# Revit family: Shower-Wall_Supply_Elbow-KOHLER-BEITOU-K-26310T
name_source: partatom
category: Plumbing Fixtures
revit_build: Autodesk Revit 2017 (Build: 20160225_1515(x64)
units: mm (PartAtom-declared; Revit-internal decimal feet)

## family parameters
Cut with Voids When Loaded = No
Host = Face
OmniClass Number = 23.31.17.00
OmniClass Title = Showers
Part Type = Normal
Room Calculation Point = No
Round Connector Dimension = Use Diameter
Shared = No

## types (7) — shared parameters
ADA Compliant = No
Assembly Code = D2010700
CW Connection = No
Cold Water Inlet = Cold Water Inlet
Date Modified = 02/09/2020
Default Elevation = 42"
Description = WALL SUPPLY
Drain Included = No
Flow Rate = 0 GPM
HW Connection = Yes
Height = 2 1/4"
Hot Water Inlet = Hot Water Inlet
Length = 4 1/8"
Manufacturer = KOHLER Co.
Master Format 2014 = 22 42 23
Master Format 2014 Name = Residential Showers
Material = Premium Metal Construction
Pressure = 0.00 psi
Product Name = BEITOU
URL = http://www.kohler.com.cn
Vent Connection = No
Waste Connection = No
Waste Water Outlet = Waste Water Outlet
WaterSense Certified = No
Width = 1 3/4"

## per-type parameters (varying)
| type | Finish | Model | Type |
| CP-Polished Chrome | Kohler-Metal-CP-Polished_Chrome | K-26310T-CP | 1 |
| 2MB-Vibrant Brushed Moderne Brass | Kohler-Metal-2MB-Vibrant_Brushed_Moderne_Brass | K-26310T-2MB | 2 |
| AF-Flange Gold | Kohler-Metal-AF-Flange_Gold | K-26310T-AF | 3 |
| BL-Matte Black | Kohler-Metal-BL-Matte_Black | K-26310T-BL | 4 |
| BN-Roman Silver | Kohler-Metal-BN-Roman_Silver | K-26310T-BN | 5 |
| RGD-Rose Gold | Kohler-Metal-RGD-Rose_Gold | K-26310T-RGD | 6 |
| SN-Champagne Gold | Kohler-Metal-SN-Champagne_Gold | K-26310T-SN | 7 |

## geometry (parser evidence)
native form markers: Sweep x5
no freeform markers — native parametric forms only
